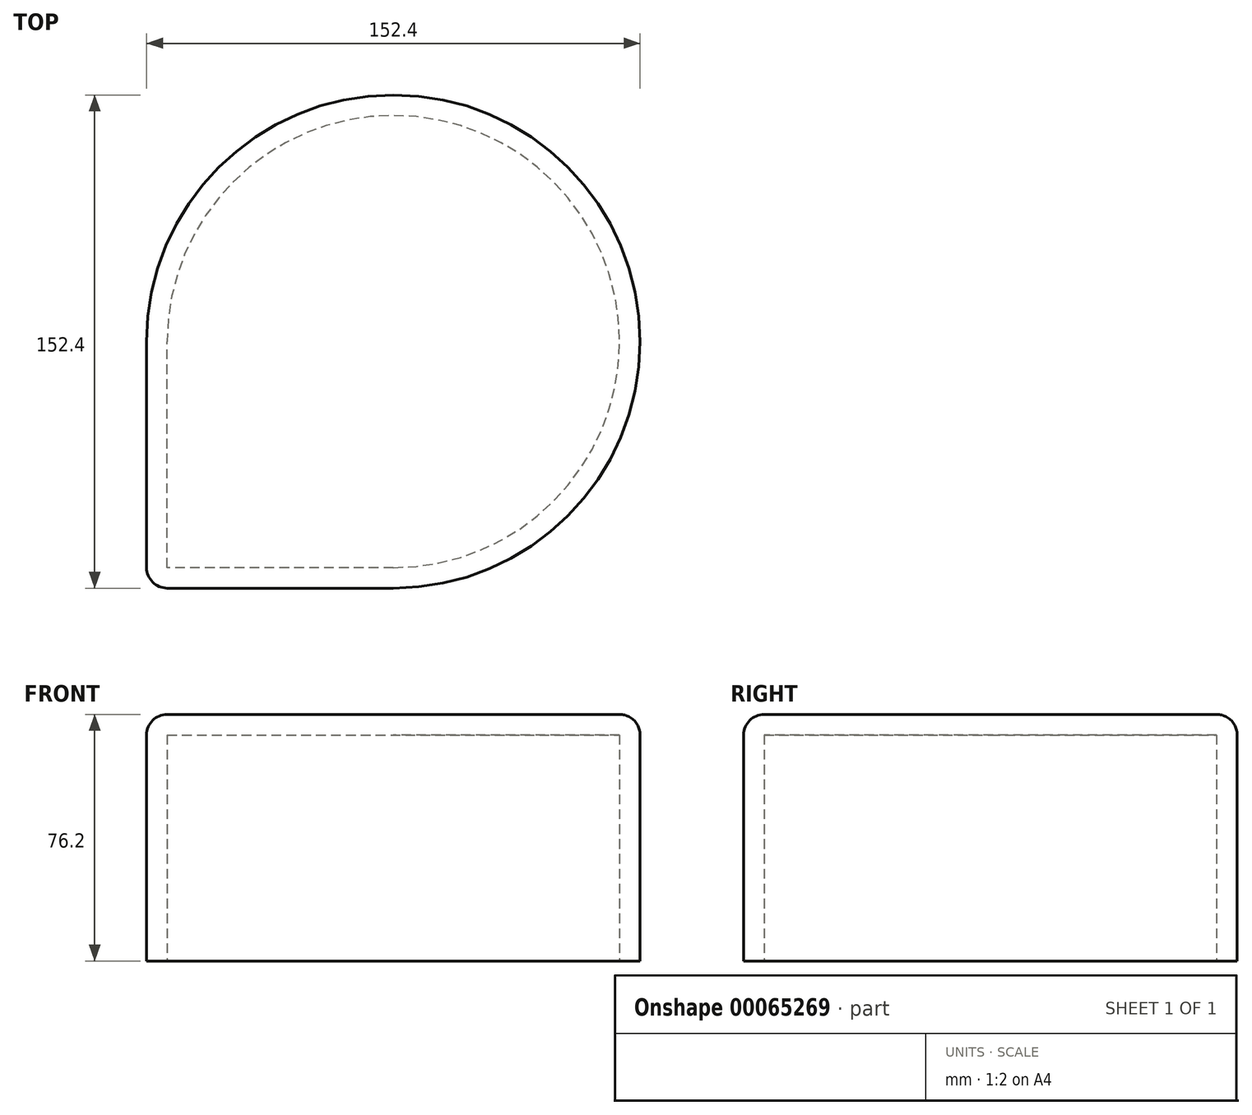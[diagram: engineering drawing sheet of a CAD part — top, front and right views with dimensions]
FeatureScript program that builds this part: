
annotation { "Feature Type Name" : "Feature", "Feature Type Description" : "" }
export const myFeature = defineFeature(function(context is Context, id is Id, definition is map)
    precondition{}
    {
        {
            var Q0;
            Q0=qCreatedBy(makeId("Front.planeOp"),FACE);
            var sketch = newSketch(context, id + "F0", { "sketchPlane" : qUnion([Q0])});
            skLineSegment(sketch, "E0.bottom", {"start": v(0, 0) * mm, "end": v(-76.2, 0) * mm});
            skLineSegment(sketch, "E0.top", {"start": v(0, 76.2) * mm, "end": v(-76.2, 76.2) * mm});
            skLineSegment(sketch, "E0.left", {"start": v(0, 0) * mm, "end": v(0, 76.2) * mm});
            skLineSegment(sketch, "E0.right", {"start": v(-76.2, 0) * mm, "end": v(-76.2, 76.2) * mm});
            skSolve(sketch);
        }
        {
            var Q0;
            Q0=makeQuery(id+"F0.imprint","IMPRINT",FACE,{"disambiguationData":[TD([[makeQuery(id+"F0.imprint","IMPRINT",EDGE,{"derivedFrom":sQuery(id+"F0.wireOp",EDGE,"E0.bottom")}),-1.0]])]});
            extrude(context, id + "F1", {"entities" : qUnion([Q0]), "depth" : 76.2 * mm});
        }
        {
            var Q0;
            Q0 = qSketchRegion(id + "F0", true);
            var Q1;
            Q1=makeQuery(id+"F1.opExtrude","CAP_EDGE",EDGE,{"disambiguationData":[OSD([sQuery(id+"F0.wireOp",EDGE,"E0.left")])],"isStart":true});
            revolve(context, id + "F2", {"operationType" : NewBodyOperationType.ADD, "entities" : qUnion([Q0]), "axis" : qUnion([Q1]), "revolveType" : RevolveType.FULL});
        }
        {
            var Q0;
            Q0=makeQuery(id+"F1.opExtrude","SWEPT_EDGE",EDGE,{"disambiguationData":[OSD([sQuery(id+"F0.wireOp",EDGE,"E0.top"),sQuery(id+"F0.wireOp",EDGE,"E0.right")])]});
            var Q1;
            Q1=makeQuery(id+"F1.opExtrude","CAP_EDGE",EDGE,{"disambiguationData":[OSD([sQuery(id+"F0.wireOp",EDGE,"E0.right")])],"isStart":false});
            fillet(context, id + "F3", {"entities" : qUnion([Q0, Q1]), "radius" : 6.35 * mm, "tangentPropagation" : true, "allowEdgeOverflow" : false});
        }
        {
            var Q0;
            {var subQ0=sQuery(id+"F0.wireOp",EDGE,"E0.bottom");Q0=makeQuery(id+"F2.boolean.opBoolean","MERGE",FACE,{"derivedFrom":[makeQuery(id+"F1.opExtrude","SWEPT_FACE",FACE,{"disambiguationData":[OSD([subQ0])]}),makeQuery(id+"F2.opRevolve","SWEPT_FACE",FACE,{"disambiguationData":[OSD([subQ0])]})]});}
            shell(context, id + "F4", {"entities" : qUnion([Q0]), "thickness" : 6.35 * mm});
        }
    });
